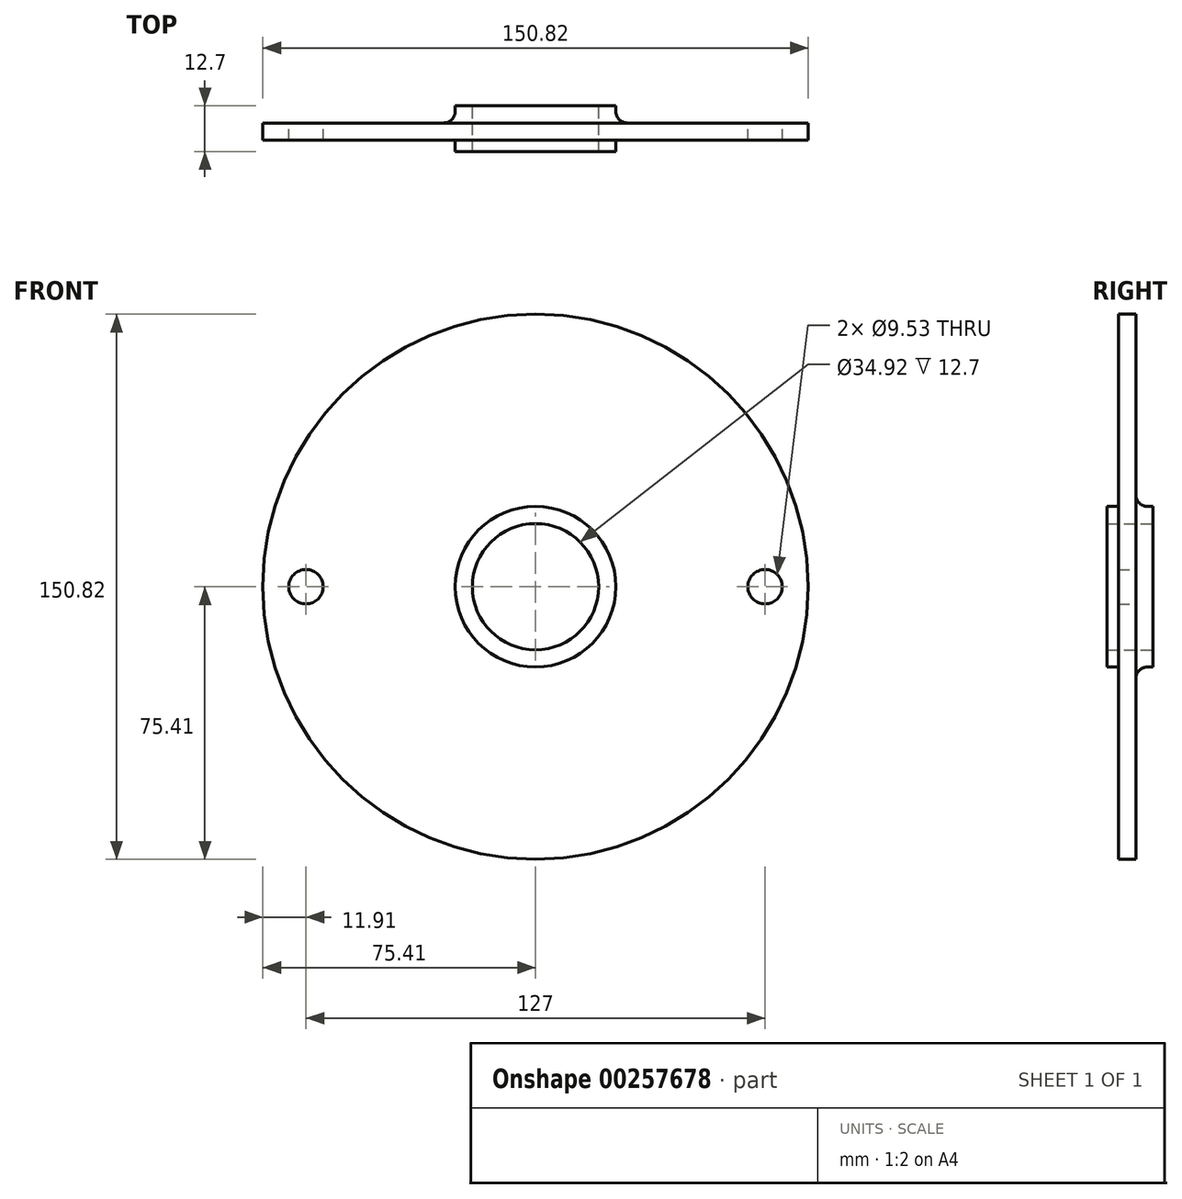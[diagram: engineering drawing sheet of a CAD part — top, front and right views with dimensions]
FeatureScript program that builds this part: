
annotation { "Feature Type Name" : "Feature", "Feature Type Description" : "" }
export const myFeature = defineFeature(function(context is Context, id is Id, definition is map)
    precondition{}
    {
        {
            var Q0;
            Q0=qCreatedBy(makeId("Front.planeOp"),FACE);
            var sketch = newSketch(context, id + "F0", { "sketchPlane" : qUnion([Q0])});
            skCircle(sketch, "E0", {"center": v(0, 0) * mm, "radius": 17.46 * mm});
            skCircle(sketch, "E1", {"center": v(0, 0) * mm, "radius": 22.23 * mm});
            skCircle(sketch, "E2", {"center": v(0, 0) * mm, "radius": 75.4 * mm});
            skCircle(sketch, "E3", {"center": v(0, 0) * mm, "radius": 63.5 * mm, "construction": true});
            skCircle(sketch, "E4", {"center": v(-63.5, 0) * mm, "radius": 4.76 * mm});
            skCircle(sketch, "E5", {"center": v(63.5, 0) * mm, "radius": 4.76 * mm});
            skSolve(sketch);
        }
        {
            var Q0;
            Q0=makeQuery(id+"F0.imprint","IMPRINT",FACE,{"disambiguationData":[TD([[makeQuery(id+"F0.imprint","IMPRINT",EDGE,{"derivedFrom":sQuery(id+"F0.wireOp",EDGE,"E0")}),-1.0]])]});
            extrude(context, id + "F1", {"entities" : qUnion([Q0]), "depth" : 12.7 * mm});
        }
        {
            var Q0;
            Q0=makeQuery(id+"F0.imprint","IMPRINT",FACE,{"disambiguationData":[TD([[makeQuery(id+"F0.imprint","IMPRINT",EDGE,{"derivedFrom":sQuery(id+"F0.wireOp",EDGE,"E1")}),-1.0]])]});
            extrude(context, id + "F2", {"entities" : qUnion([Q0]), "operationType" : NewBodyOperationType.ADD, "depth" : 9.52 * mm, "hasSecondDirection" : true, "secondDirectionOppositeDirection" : false, "secondDirectionDepth" : 4.76 * mm});
        }
        {
            var Q0;
            Q0=makeQuery(id+"F2.opExtrude","CAP_EDGE",EDGE,{"disambiguationData":[OSD([sQuery(id+"F0.wireOp",EDGE,"E1")])],"isStart":false});
            var Q1;
            Q1=makeQuery(id+"F2.opExtrude","CAP_EDGE",EDGE,{"disambiguationData":[OSD([sQuery(id+"F0.wireOp",EDGE,"E1")])],"isStart":true});
            fillet(context, id + "F3", {"entities" : qUnion([Q0, Q1]), "radius" : 3.17 * mm, "tangentPropagation" : true, "allowEdgeOverflow" : false});
        }
    });
